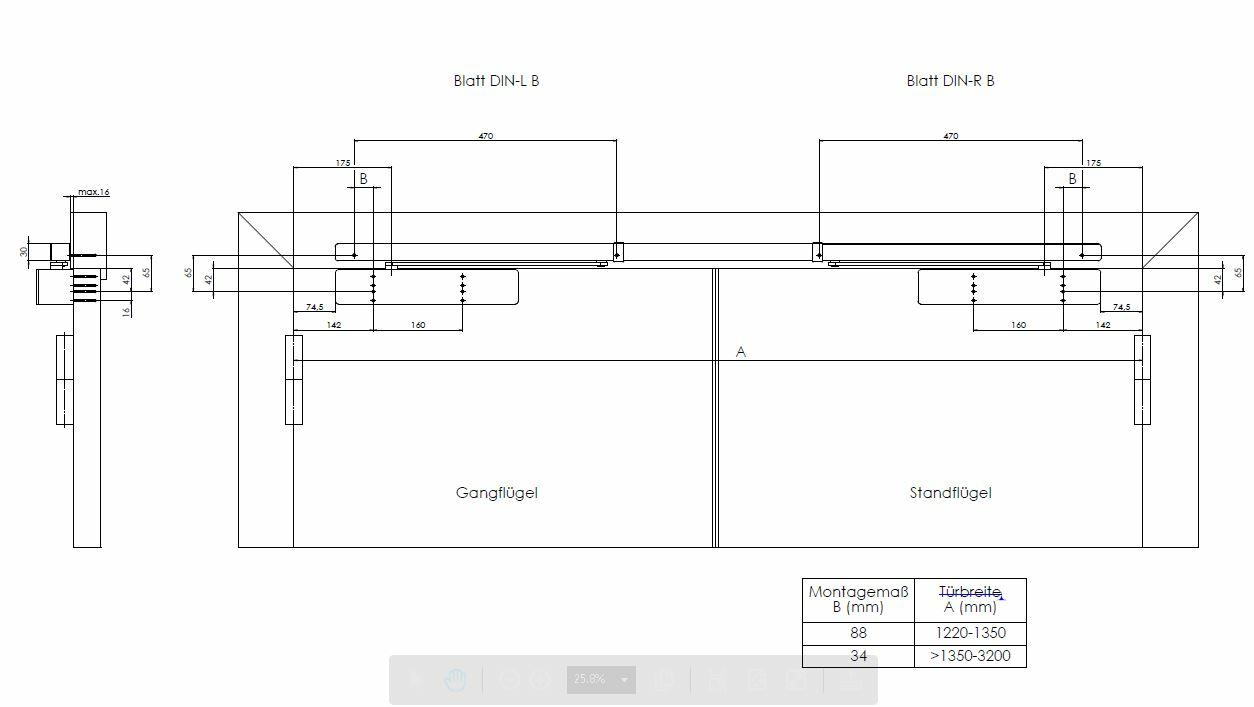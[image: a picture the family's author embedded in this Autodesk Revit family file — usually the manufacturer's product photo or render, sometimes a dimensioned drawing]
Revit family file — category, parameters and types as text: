
# Revit family: Doors - Hardware_Double-Door_Dormakaba_TS98-GSR-EMF-XEA
name_source: partatom
category: Allgemeines Modell
revit_build: Autodesk Revit 2016 (Build: 20150220_1215(x64)
units: mm (PartAtom-declared; Revit-internal decimal feet)

## family parameters
Basisbauteil = Fläche
Beim Laden mit Abzugskörper schneiden = Nein
Bemaßung runder Anschluss = Durchmesser verwenden
Gemeinsam genutzt = Nein
Kann Basisbauteil für Bewehrung sein = Nein
OmniClass-Nummer = 23.30.40.11.27.11
OmniClass-Titel = Door Closers
Raumberechnungspunkt = Nein
Teiletyp = Normal

## types (1)
- Doors - Hardware_Double-Door_Dormakaba_TS98-GSR-EMF-XEA
    Brand url = http://www.dormakaba.com
    Depth Jamb to Door = 0 mm  [stored 0 ft]
    Design country = Germany
    Door Closers Types = TS98-GSR-EMF-XEA-Pull-Side-Door_Fixing
    Edition number = 1
    Extension Height = 17 mm
    Hinge Distance = 1800 mm  [stored 5.90551 ft]
    Manufacturer country = Germany
    Manufacturer name = DORMA
    Material main = Aluminium
    Material secondary = Zink
    Max Depth Jamb to Door = 0 mm  [stored 0 ft]
    NBS Reference Code = 25-38-20-20
    NBS Reference Description = Door Hardware Systems
    Nominal height = 30 mm  [stored 0.0984252 ft]
    Nominal width = 3051 mm  [stored 10.0098 ft]
    OmniClass Code = 23-17 19 11 19 11
    OmniClass Description = Door Closers
    Opening Angle = 0.00°
    Primary Material = Aluminium-Dormakaba-Anodized Silver
    Product SKU = g-sr_emf_xea
    Product url = http://www.dorma.com
    Pull Side Door = TS98-GSR-EMF-XEA-Pull-Side-Door_Fixing
    Push side = TS98-GSR-EMF-XEA_Push-Side-Door_Fixing
    Uniclass 1.4 Code = L41812
    Uniclass 1.4 Description = Door closers
    Uniclass 2015 Code = Pr_30_36_59_92
    Uniclass 2015 Name = Uncontrolled door closers
    Vorgabe-Ansicht = 1219 mm
    Weight Net (Kg) = 3.7

note: [stored X ft] marks values corroborated as IEEE doubles in the binary element streams (Revit-internal decimal feet)

## geometry (parser evidence)
native form markers: Blend x2, Sweep x17
no freeform markers — native parametric forms only
